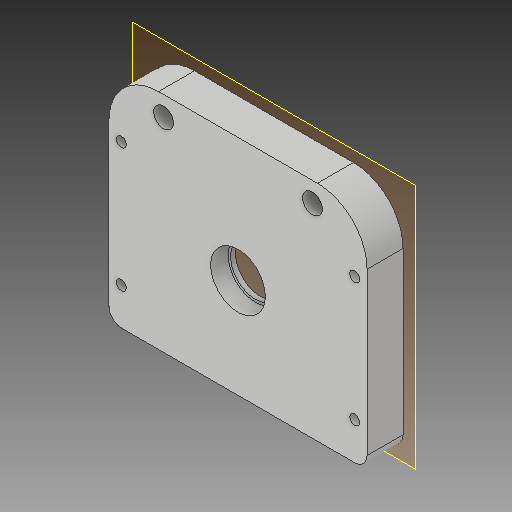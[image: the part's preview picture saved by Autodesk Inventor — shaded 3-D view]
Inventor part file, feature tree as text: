
AUTODESK INVENTOR PART (.ipt)
format: ipt  version: 2017 (Build 210142000, 142)  size: 181,760 bytes
history: native  units: mm
features: extrude x4, sketch x4, reference x2, projected_geometry x2, other x2, plane x1
ambient origin geometry x8: Origin, YZ Plane, XZ Plane, XY Plane, X Axis, Y Axis, Z Axis, Center Point
bodies: Solid1 (feature_tree)
feature tree (15):
  plane  "Work Plane1"
  extrude  "Extrusion1"  Depth=5.5mm TaperAngle=0.0deg
  extrude  "Extrusion2"  Depth=2.0mm TaperAngle=0.0deg
  extrude  "Extrusion3"  Depth=7.0mm TaperAngle=0.0deg
  extrude  "Extrusion4"  Depth=7.0mm
  sketch  "Sketch1"  dims[d0=76.0mm d1=5.5mm d2=0.0mm]
  reference  "Reference1"
  sketch  "Sketch2"  dims[d3=20.0mm d4=2.0mm d5=0.0mm]
  projected_geometry  "Projected Loop1"
  sketch  "Sketch3"  dims[d6=22.0mm d7=7.0mm d8=0.0mm]
  projected_geometry  "Projected Loop2"
  sketch  "Sketch4"  dims[d9=8.0mm d10=8.0mm d11=60.0mm d12=7.0mm d13=0.0mm]
  reference  "Reference2"
  other  "peristaltic pump.iam"
  other  "frame top:1"
